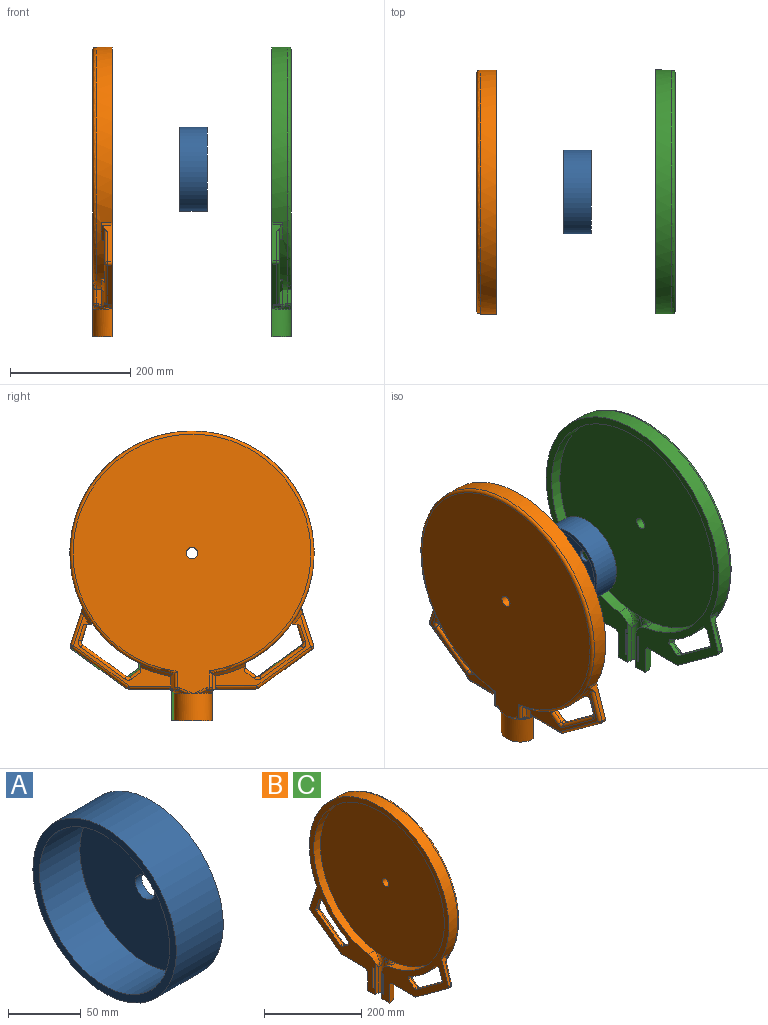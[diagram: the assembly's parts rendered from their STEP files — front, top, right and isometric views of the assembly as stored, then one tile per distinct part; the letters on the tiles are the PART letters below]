
ASSEMBLY  parts=3 mates=2
PART A: 6 faces, bbox 45.7x139.7x139.7 mm
  f0: cylinder r=63.5mm len=127mm, axis (-1,0,0), area 15707.9mm2, adj f3,f5
  f1: cylinder r=69.85mm len=139.7mm, axis (-1,0,0), area 20065.6mm2, adj f2,f3
  f2: plane 139.7x139.7mm, normal (1,0,0), area 15042.9mm2, adj f1,f4
  f3: plane 139.7x139.7mm, normal (-1,0,0), area 2660.2mm2, adj f0,f1
  f4: cylinder r=9.53mm len=19.05mm, axis (-1,0,0), area 380mm2, adj f2,f5
  f5: plane 127x127mm, normal (-1,0,0), area 12382.7mm2, adj f0,f4
PART B: 110 faces, bbox 54.1x443.7x503.1 mm
  f0: plane 2.37x0.11mm, normal (0,-1,0), area 0.2mm2, adj f9,f62,f77
  f1: plane 6.09x0.71mm, normal (0,1,0), area 2.7mm2, adj f9,f59,f71
  f2: plane 25.78x8.89mm, normal (0,1,0), area 211.5mm2, adj f3,f53,f59,f60,f68
  f3: cylinder r=203.2mm len=406.4mm, axis (-1,0,0), area 29083.5mm2, adj f2,f7,f9,f54,f65,f66,f67,f69
  f4: bspline ~23.86x11.27mm, area 129mm2, adj f5,f12,f23,f32
  f5: bspline ~26.07x25.11mm, area 212.1mm2, adj f4,f12,f23,f31
  f6: plane 63.5x31.75mm, normal (0,0,-1), area 1253.2mm2, adj f9,f23,f24,f25,f26,f27
  f7: plane 25.2x8.89mm, normal (0,-1,0), area 206.4mm2, adj f3,f55,f62,f63,f75
  f8: cylinder r=190.5mm len=381mm, axis (-1,0,0), area 21917.7mm2, adj f9,f12,f30,f31,f33
  f9: plane 486.37x410.18mm, normal (-1,0,0), area 28188.3mm2, adj f0,f1,f3,f6,f8,f13,f14,f15
  f10: cylinder r=9.53mm len=19.05mm, axis (-1,0,0), area 744.9mm2, adj f11,f12
  f11: plane 431.79x396.24mm, normal (1,0,0), area 124659.7mm2, adj f10,f50,f51,f52,f53,f54,f55,f56
  f12: plane 382.48x382.48mm, normal (-1,0,0), area 113724.4mm2, adj f4,f5,f8,f10,f32
  f13: plane 50.8x3.18mm, normal (0,1,0), area 161.3mm2, adj f9,f14,f16,f17
  f14: plane 3.18x3.18mm, normal (0,0,1), area 10.1mm2, adj f9,f13,f15,f17
  f15: plane 50.8x3.18mm, normal (0,-1,0), area 161.3mm2, adj f9,f14,f16,f17
  f16: plane 3.18x3.18mm, normal (0,0,-1), area 10.1mm2, adj f9,f13,f15,f17
  f17: plane 50.8x3.18mm, normal (-1,0,0), area 161.3mm2, adj f13,f14,f15,f16
  f18: plane 3.18x3.18mm, normal (0,0,1), area 10.1mm2, adj f9,f19,f21,f22
  f19: plane 50.8x3.18mm, normal (0,-1,0), area 161.3mm2, adj f9,f18,f20,f22
  f20: plane 3.18x3.18mm, normal (0,0,-1), area 10.1mm2, adj f9,f19,f21,f22
  f21: plane 50.8x3.18mm, normal (0,1,0), area 161.3mm2, adj f9,f18,f20,f22
  f22: plane 50.8x3.18mm, normal (-1,0,0), area 161.3mm2, adj f18,f19,f20,f21
  f23: cylinder r=9.65mm len=86.37mm, axis (0,0,-1), area 2272.2mm2, adj f4,f5,f6,f24,f26,f31,f32,f33
  f24: plane 91.76x22.08mm, normal (-1,0,0), area 5.7mm2, adj f6,f23,f25,f30,f33
  f25: plane 66.08x9.53mm, normal (0,1,0), area 629.4mm2, adj f6,f9,f24,f30
  f26: plane 79.64x9.3mm, normal (0,-1,0), area 620.3mm2, adj f6,f9,f23,f31
  f27: cylinder r=31.75mm len=63.5mm, axis (0,0,-1), area 4582.2mm2, adj f6,f9,f48,f49,f50,f57,f59,f62
  f28: plane 1.27x1.27mm, normal (0,0,-1), area 0.8mm2, adj f49,f52,f60
  f29: plane 1.27x1.27mm, normal (0,0,-1), area 0.8mm2, adj f48,f56,f63
  f30: cylinder r=25.4mm len=25.1mm, axis (-1,0,0), area 342.6mm2, adj f8,f9,f24,f25
  f31: bspline ~38.35x26.48mm, area 518mm2, adj f5,f8,f9,f23,f26
  f32: bspline ~26.39x25.15mm, area 213.3mm2, adj f4,f12,f23,f33
  f33: bspline ~25.44x22.53mm, area 200.2mm2, adj f8,f23,f24,f32
  f34: plane 73.18x53.17mm, normal (0,0.59,0.81), area 689.3mm2, adj f9,f89,f92,f95
  f35: plane 28.05x9.11mm, normal (0,0.95,-0.31), area 224.7mm2, adj f9,f81,f93,f95
  f36: plane 60.14x19.69mm, normal (0,-0.95,0.31), area 533.2mm2, adj f9,f79,f80,f82,f83
  f37: plane 92.75x67.38mm, normal (0,-0.59,-0.81), area 873.6mm2, adj f9,f82,f85,f86
  f38: plane 69.84x13.07mm, normal (0,0,-1), area 543.2mm2, adj f9,f76,f77,f78,f85,f88
  f39: plane 17.56x12.76mm, normal (0,-0.59,0.81), area 165.4mm2, adj f9,f73,f89,f90
  f40: plane 162.22x117.92mm, normal (1,0,0), area 2309.5mm2, adj f73,f74,f75,f80,f81,f83,f86,f88
  f41: plane 70.43x13.66mm, normal (0,0,-1), area 542.7mm2, adj f9,f68,f71,f72,f100,f102
  f42: plane 89.11x64.74mm, normal (0,0.59,-0.81), area 839.3mm2, adj f9,f97,f99,f100
  f43: plane 61.38x20.09mm, normal (0,0.95,0.31), area 542.7mm2, adj f9,f66,f67,f96,f97
  f44: plane 29.46x9.57mm, normal (0,-0.95,-0.31), area 236.1mm2, adj f9,f65,f103,f104
  f45: plane 69.54x50.53mm, normal (0,-0.59,0.81), area 655mm2, adj f9,f103,f106,f109
  f46: plane 18.53x13.46mm, normal (0,0.59,0.81), area 174.5mm2, adj f9,f70,f107,f109
  f47: plane 158.58x116.6mm, normal (1,0,0), area 2313.3mm2, adj f65,f66,f68,f69,f70,f96,f99,f102
  f48: cone r=31.75mm half-angle=45deg, axis (0,0,1), area 140.7mm2, adj f27,f29,f56,f58,f62,f63
  f49: cone r=31.75mm half-angle=45deg, axis (0,0,1), area 140.7mm2, adj f27,f28,f51,f52,f59,f60
  f50: bspline ~11.84x4.1mm, area 13.5mm2, adj f11,f27,f51
  f51: bspline ~20.52x11.7mm, area 68.3mm2, adj f11,f49,f50,f52
  f52: cylinder r=5.08mm len=5.08mm, axis (0,-1,0), area 25.8mm2, adj f11,f28,f49,f51,f61
  f53: cylinder r=5.08mm len=27.45mm, axis (0,0,-1), area 201.7mm2, adj f2,f11,f54,f61
  f54: torus R=198.12mm, axis (1,0,0), area 9626.2mm2, adj f3,f11,f53,f55
  f55: cylinder r=5.08mm len=26.96mm, axis (0,0,1), area 197.4mm2, adj f7,f11,f54,f64
  f56: cylinder r=5.08mm len=5.08mm, axis (0,-1,0), area 25.8mm2, adj f11,f29,f48,f58,f64
  f57: bspline ~10.18x3.59mm, area 13.5mm2, adj f11,f27,f58
  f58: bspline ~20.52x11.7mm, area 68.3mm2, adj f11,f48,f56,f57
  f59: bspline ~30.04x13.28mm, area 72.1mm2, adj f1,f2,f27,f49,f60,f68,f72
  f60: cylinder r=5.08mm len=5.08mm, axis (1,0,0), area 25.8mm2, adj f2,f28,f49,f59,f61
  f61: sphere r=5.08mm, area 25.8mm2, adj f52,f53,f60
  f62: bspline ~30.22x12.78mm, area 68.9mm2, adj f0,f7,f27,f48,f63,f76,f78
  f63: cylinder r=5.08mm len=5.08mm, axis (1,0,0), area 25.8mm2, adj f7,f29,f48,f62,f64
  f64: sphere r=5.08mm, area 40.5mm2, adj f55,f56,f63
  f65: plane 18.85x15.67mm, normal (0,-0.15,-0.99), area 135.9mm2, adj f3,f9,f44,f47,f66,f104
  f66: cone r=203.2mm half-angle=45deg, axis (-1,0,0), area 211.6mm2, adj f3,f43,f47,f65,f67,f96
  f67: plane 17.81x3.83mm, normal (0,1,-0.07), area 65.1mm2, adj f3,f9,f43,f66
  f68: plane 30.41x12.96mm, normal (0.71,0.71,0), area 186mm2, adj f2,f41,f47,f59,f69,f72,f102
  f69: cone r=203.2mm half-angle=45deg, axis (-1,0,0), area 398.8mm2, adj f3,f47,f68,f70
  f70: plane 19.06x15.86mm, normal (0,1,-0.09), area 132.1mm2, adj f3,f9,f46,f47,f69,f107
  f71: plane 6.06x5.08mm, normal (0,0.71,-0.71), area 43.5mm2, adj f1,f9,f41,f72
  f72: bspline ~14.24x5.84mm, area 65.1mm2, adj f41,f59,f68,f71
  f73: plane 19.04x15.84mm, normal (0,-1,-0.09), area 132.5mm2, adj f3,f9,f39,f40,f74,f90
  f74: cone r=203.2mm half-angle=45deg, axis (-1,0,0), area 404.4mm2, adj f3,f40,f73,f75
  f75: plane 26.84x10.39mm, normal (0.71,-0.71,0), area 172.1mm2, adj f7,f40,f74,f76,f88
  f76: bspline ~13.01x12.33mm, area 12.8mm2, adj f38,f62,f75,f78,f88
  f77: plane 5.08x5.08mm, normal (0,-0.71,-0.71), area 17mm2, adj f0,f9,f38,f78
  f78: bspline ~15.42x5.65mm, area 85.6mm2, adj f38,f62,f76,f77
  f79: plane 17.81x3.81mm, normal (0,-1,-0.07), area 64.7mm2, adj f3,f9,f36,f80
  f80: cone r=203.2mm half-angle=45deg, axis (-1,0,0), area 212.5mm2, adj f3,f36,f40,f79,f81,f83
  f81: plane 18.85x15.67mm, normal (0,0.15,-0.99), area 136mm2, adj f3,f9,f35,f40,f80,f93
  f82: cylinder r=5.08mm len=7.62mm, axis (-1,0,0), area 48.6mm2, adj f9,f36,f37,f84
  f83: cylinder r=5.08mm len=52.1mm, axis (0,0.31,0.95), area 415.1mm2, adj f36,f40,f80,f84
  f84: sphere r=5.08mm, area 32.4mm2, adj f82,f83,f86
  f85: cylinder r=5.08mm len=7.62mm, axis (-1,0,0), area 24.3mm2, adj f9,f37,f38,f87
  f86: cylinder r=5.08mm len=95.73mm, axis (0,-0.81,0.59), area 914.8mm2, adj f37,f40,f84,f87
  f87: sphere r=5.08mm, area 16.2mm2, adj f85,f86,f88
  f88: cylinder r=5.08mm len=69.47mm, axis (0,-1,0), area 536mm2, adj f38,f40,f75,f76,f87
  f89: cylinder r=5.08mm len=7.62mm, axis (-1,0,0), area 48.6mm2, adj f9,f34,f39,f91
  f90: cylinder r=5.08mm len=20.55mm, axis (0,0.81,0.59), area 161.2mm2, adj f39,f40,f73,f91
  f91: torus R=10.16mm, axis (1,0,0), area 69.5mm2, adj f40,f89,f90,f92
  f92: cylinder r=5.08mm len=76.17mm, axis (0,0.81,-0.59), area 721.8mm2, adj f34,f40,f91,f94
  f93: cylinder r=5.08mm len=29.62mm, axis (0,-0.31,-0.95), area 225.2mm2, adj f35,f40,f81,f94
  f94: torus R=10.16mm, axis (1,0,0), area 69.5mm2, adj f40,f92,f93,f95
  f95: cylinder r=5.08mm len=7.62mm, axis (1,0,0), area 48.6mm2, adj f9,f34,f35,f94
  f96: cylinder r=5.08mm len=53.42mm, axis (0,0.31,-0.95), area 426.1mm2, adj f43,f47,f66,f98
  f97: cylinder r=5.08mm len=7.62mm, axis (-1,0,0), area 48.6mm2, adj f9,f42,f43,f98
  f98: sphere r=5.08mm, area 25.8mm2, adj f96,f97,f99
  f99: cylinder r=5.08mm len=92.1mm, axis (0,-0.81,-0.59), area 878.9mm2, adj f42,f47,f98,f101
  f100: cylinder r=5.08mm len=7.62mm, axis (-1,0,0), area 24.3mm2, adj f9,f41,f42,f101
  f101: sphere r=5.08mm, area 13.6mm2, adj f99,f100,f102
  f102: cylinder r=5.08mm len=69.47mm, axis (0,-1,0), area 534.1mm2, adj f41,f47,f68,f101
  f103: cylinder r=5.08mm len=7.62mm, axis (1,0,0), area 48.6mm2, adj f9,f44,f45,f105
  f104: cylinder r=5.08mm len=31.03mm, axis (0,-0.31,0.95), area 237mm2, adj f44,f47,f65,f105
  f105: torus R=10.16mm, axis (1,0,0), area 69.5mm2, adj f47,f103,f104,f106
  f106: cylinder r=5.08mm len=72.53mm, axis (0,0.81,0.59), area 685.9mm2, adj f45,f47,f105,f108
  f107: cylinder r=5.08mm len=21.51mm, axis (0,0.81,-0.59), area 170.6mm2, adj f46,f47,f70,f108
  f108: torus R=10.16mm, axis (1,0,0), area 69.5mm2, adj f47,f106,f107,f109
  f109: cylinder r=5.08mm len=7.62mm, axis (-1,0,0), area 48.6mm2, adj f9,f45,f46,f108
PART C: same geometry as B
PLACE A t=(-153.42,-598.88,0)mm
PLACE B rot(axis=(0,0,1),180deg) t=(-266.19,0,0)mm
PLACE C at identity
MATE fastened B.f3 <-> C.f3  axis (1,0,0) through (-285.5,0,0)mm
MATE fastened A.f0 <-> C.f3  axis (1,0,0) through (-107.7,0,0)mm
